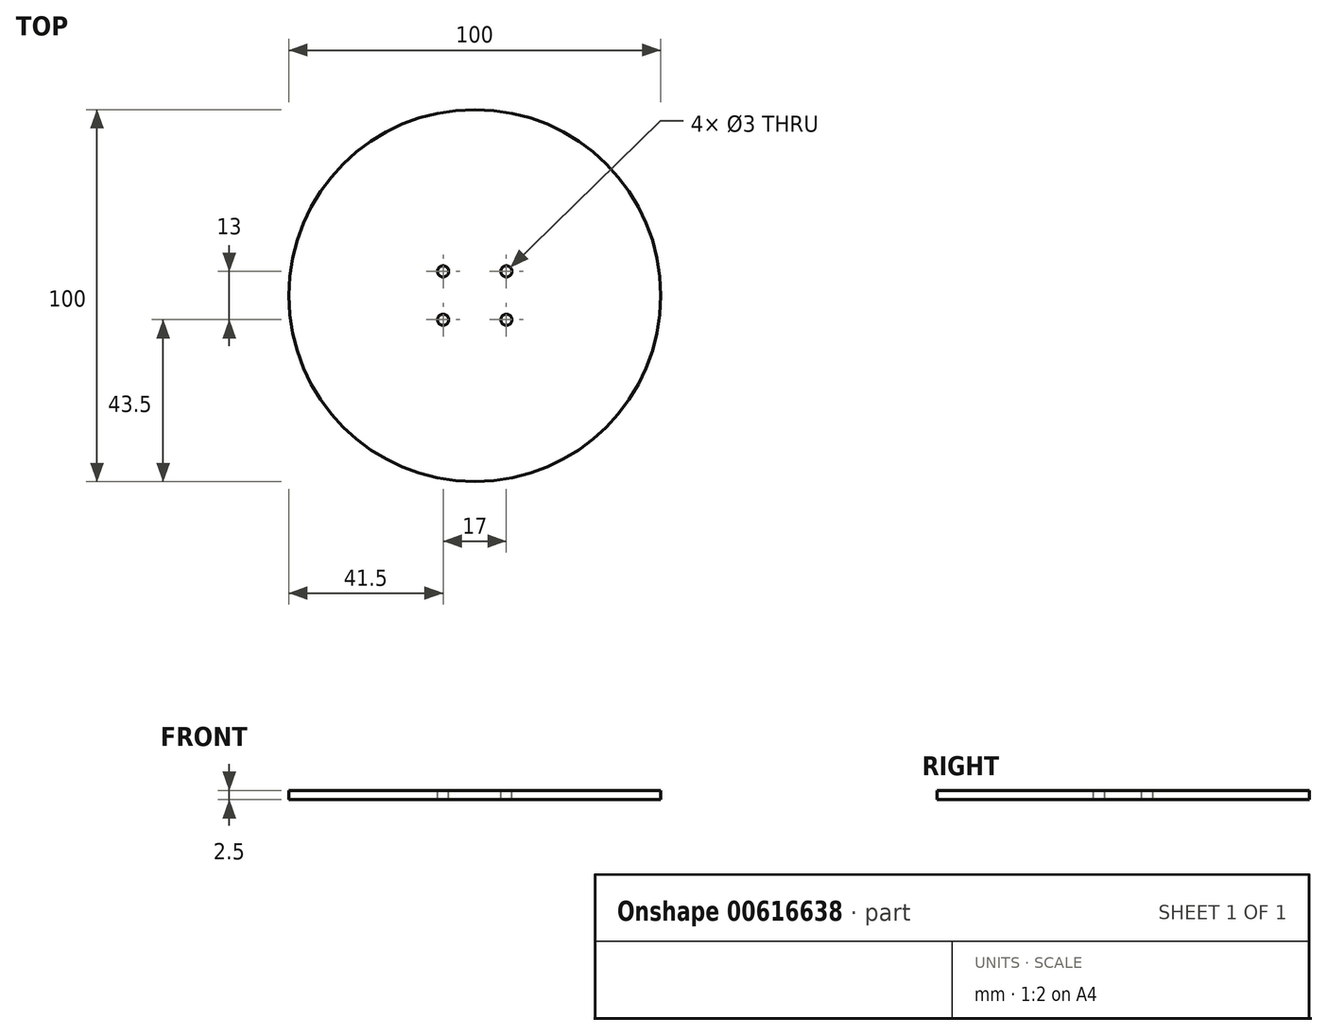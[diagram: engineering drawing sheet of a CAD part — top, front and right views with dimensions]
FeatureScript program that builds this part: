
annotation { "Feature Type Name" : "Feature", "Feature Type Description" : "" }
export const myFeature = defineFeature(function(context is Context, id is Id, definition is map)
    precondition{}
    {
        {
            var Q0;
            Q0=qCreatedBy(makeId("Top.planeOp"),FACE);
            var sketch = newSketch(context, id + "F0", { "sketchPlane" : qUnion([Q0])});
            skCircle(sketch, "E0", {"center": v(0, 0) * mm, "radius": 50 * mm});
            skCircle(sketch, "E1", {"center": v(-8.5, 6.5) * mm, "radius": 1.5 * mm});
            skCircle(sketch, "E2", {"center": v(-8.5, -6.5) * mm, "radius": 1.5 * mm});
            skCircle(sketch, "E3", {"center": v(8.5, 6.5) * mm, "radius": 1.5 * mm});
            skCircle(sketch, "E4", {"center": v(8.5, -6.5) * mm, "radius": 1.5 * mm});
            skSolve(sketch);
        }
        {
            var Q0;
            Q0 = qSketchRegion(id + "F0", true);
            extrude(context, id + "F1", {"entities" : qUnion([Q0]), "oppositeDirection" : true, "depth" : 2.5 * mm, "offsetDistance" : 25 * mm});
        }
    });
